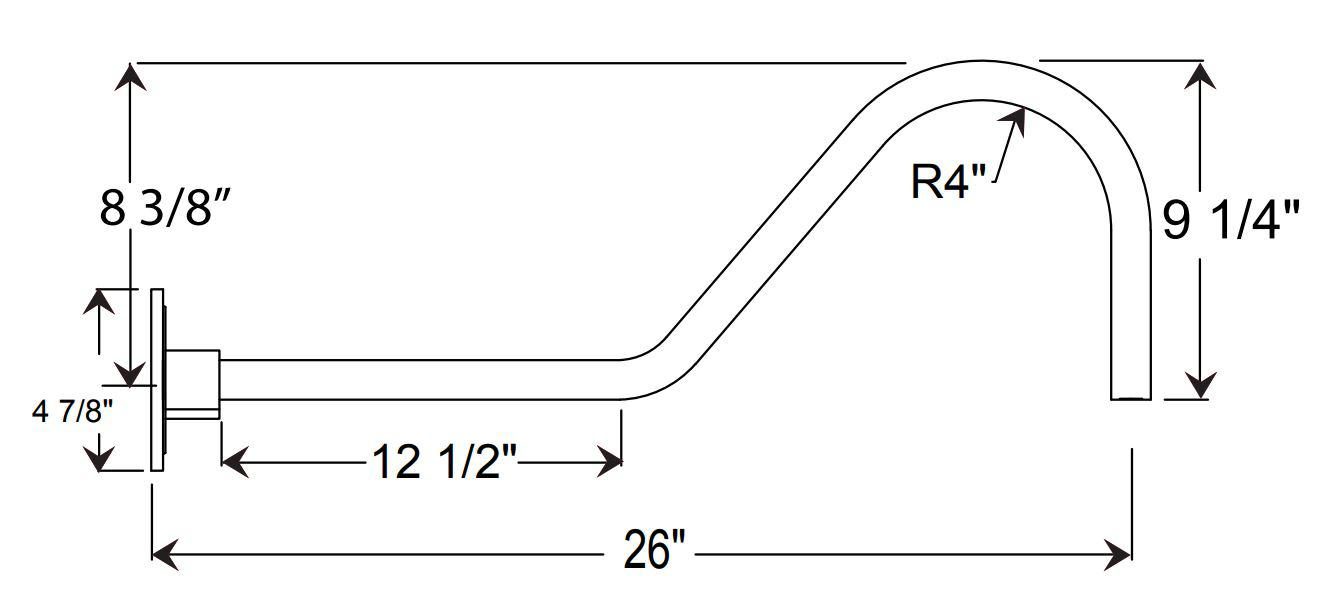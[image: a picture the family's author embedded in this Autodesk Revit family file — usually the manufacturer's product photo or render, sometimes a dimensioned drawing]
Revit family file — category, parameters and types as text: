
# Revit family: Euro Barn Slim EU9  (14,16,18,20,22) LED
name_source: partatom
category: Lighting Fixtures
units: mm (PartAtom-declared; Revit-internal decimal feet)

## family parameters
Always vertical = Yes
Cut with Voids When Loaded = No
Light Source = Yes
OmniClass Number = 23.80.70.00
OmniClass Title = Lighting
Part Type = Normal
Room Calculation Point = No
Round Connector Dimension = Use Diameter
Shared = No
Work Plane-Based = No

## types (5) — shared parameters
Apparent Load = 200 VA
Body Colour = Spun aluminium
Body Material = body
CRI = >90
Color Filter = 16777215
Construction Material = Heavy Duty spun aluminum.
Default Elevation = 0' - 0"
Description = 120-277 Voltage
Dimming = 1%
Dimming Lamp Color Temperature Shift = <None>
Efficiency = 65-125 lumens per watt
Fixture Finish = Fixture finish
Lamp = MB
Life = L70 50,000 hours
Load Classification = Lighting
Manufacturer = ANP Lighting
Mounting Finish = Mounting finish
Photometric Web File = generic.ies
Power Factor = 1
Tilt Angle = 90.00°
URL = https://www.anplighting.com
Voltage = 277 V
Warranty = 5 year limited warranty
Wattage Comments = 200W Max

## per-type parameters (varying)
| type | EU914 | EU916 | EU918 | EU920 | EU922 | Fixture Diameter | Fixture Height | Weight |
| EU914 | Yes | No | No | No | No | 1' - 2" | 0' - 5" | 3.2 lbs |
| EU916 | No | Yes | No | No | No | 1' - 4" | 0' - 5" | 3.7 lbs |
| EU918 | No | No | Yes | No | No | 1' - 6" | 0' - 5" | 4.7 lbs |
| EU920 | No | No | No | Yes | No | 1' - 8" | 0' - 5" | 5.2 lbs |
| EU922 | No | No | No | No | Yes | 1' - 10" | 0' - 5 1/2" | 5.7 lbs |

note: column(s) folded — value = type name in every type: Model

## geometry (parser evidence)
native form markers: Sweep x41
no freeform markers — native parametric forms only
